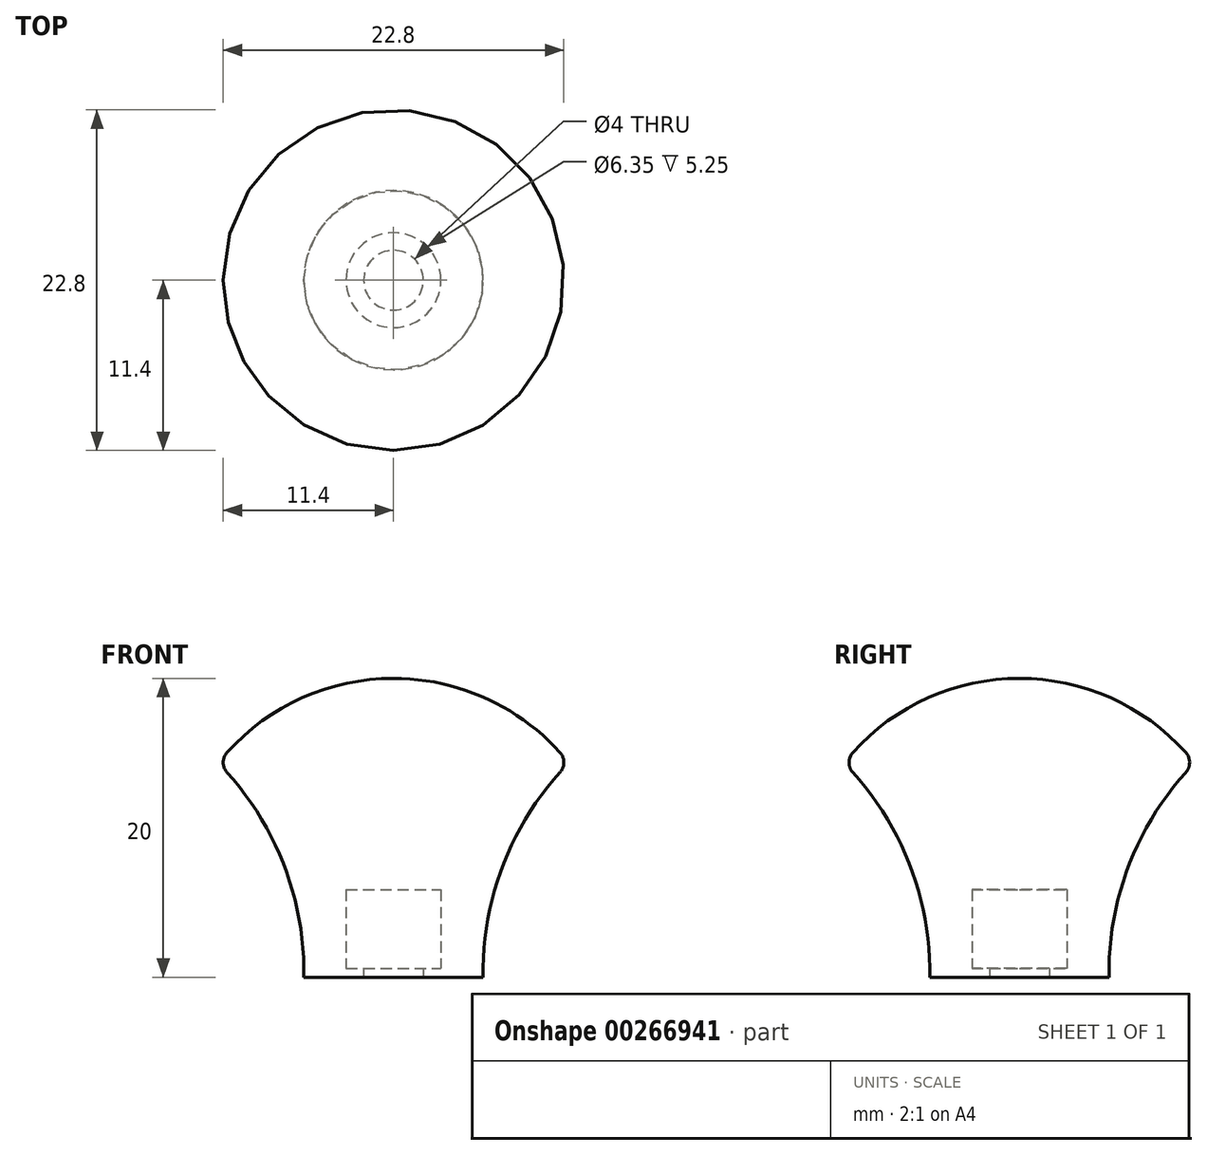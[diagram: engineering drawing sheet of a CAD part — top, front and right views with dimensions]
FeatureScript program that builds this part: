
annotation { "Feature Type Name" : "Feature", "Feature Type Description" : "" }
export const myFeature = defineFeature(function(context is Context, id is Id, definition is map)
    precondition{}
    {
        {
            var Q0;
            Q0=qCreatedBy(makeId("Front.planeOp"),FACE);
            var sketch = newSketch(context, id + "F0", { "sketchPlane" : qUnion([Q0])});
            skLineSegment(sketch, "E0", {"start": v(0, 0) * mm, "end": v(0, 20) * mm, "construction": true});
            skLineSegment(sketch, "E1", {"start": v(-6, 0) * mm, "end": v(-2, 0) * mm});
            skLineSegment(sketch, "E2", {"start": v(-2, 0) * mm, "end": v(-2, 0.6) * mm});
            skLineSegment(sketch, "E3", {"start": v(-2, 0.6) * mm, "end": v(-3.17, 0.6) * mm});
            skLineSegment(sketch, "E4", {"start": v(-3.17, 0.6) * mm, "end": v(-3.17, 5.85) * mm});
            skLineSegment(sketch, "E5", {"start": v(-3.17, 5.85) * mm, "end": v(0, 5.85) * mm});
            skArc(sketch, "E6", {"start": v(-6, 0) * mm, "mid": v(-7.27, 7.34) * mm, "end": v(-11.14, 13.7) * mm});
            skArc(sketch, "E7", {"start": v(-11.14, 15.04) * mm, "mid": v(-11.4, 14.37) * mm, "end": v(-11.14, 13.7) * mm});
            skArc(sketch, "E8", {"start": v(0, 20) * mm, "mid": v(-6.1, 18.7) * mm, "end": v(-11.14, 15.04) * mm});
            skLineSegment(sketch, "E9", {"start": v(0, 5.85) * mm, "end": v(0, 20) * mm});
            skSolve(sketch);
        }
        {
            var Q0;
            Q0=makeQuery(id+"F0.imprint","IMPRINT",FACE,{"disambiguationData":[TD([[makeQuery(id+"F0.imprint","IMPRINT",EDGE,{"derivedFrom":sQuery(id+"F0.wireOp",EDGE,"E1")}),1.0]])]});
            var Q1;
            Q1=sQuery(id+"F0.wireOp",EDGE,"E0");
            revolve(context, id + "F1", {"entities" : qUnion([Q0]), "axis" : qUnion([Q1]), "revolveType" : RevolveType.FULL});
        }
    });
